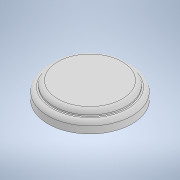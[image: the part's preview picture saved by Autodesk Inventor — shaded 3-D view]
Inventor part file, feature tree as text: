
AUTODESK INVENTOR PART (.ipt)
format: ipt  version: 2022 (Build 260153000, 153)  size: 133,632 bytes
history: native  units: mm
features: revolve x1, fillet x1, sketch x1
ambient origin geometry x8: Origin, YZ Plane, XZ Plane, XY Plane, X Axis, Y Axis, Z Axis, Center Point
bodies: Solid1 (feature_tree)
feature tree (3):
  revolve  "Revolution1"  [1 undecoded]
  fillet  "Fillet1"  Radius=1.0mm
  sketch  "Sketch1"  dims[d1=2.0mm d2=1.0mm d3=1.0mm d4=90.0deg d5=0.75mm d6=15.0mm]
note: 1 required parameter value undecoded (feature->parameter linkage not recoverable at this tier; creation-order binding heuristic only, values carry confidence <= 0.55)
